# Revit family: BTSMP-LMI
name_source: partatom
category: Communication Devices
revit_build: Autodesk Revit 2014 (Build: 20130308_1515(x64)
units: mm (PartAtom-declared; Revit-internal decimal feet)

## types (1)
- BTSMP
    Assembly Code = D5090
    Black = Paint - Hubbell - Carbon Black
    Certifications = • Conforms with UL STD 508, UL STD 244A
    Coverage = 1:1 (Mounting Height : Coverage Radius);
Up to 14ft
    Default Elevation = 48 "
    Description = The Passive-Infrared Bluetooth sensor module, or BTSMP, is the newest series of the Hubbell Control Solutions Bluetooth Sensor family. Perfect for architectural applications, it is smaller, more cost effective, seamlessly integrates with all luminaires and provides simple dimming control using the controlHUBB app.
    Features = Passive Infrared (PIR) sensing technology provides excellent major
motion detection
• Wireless programming using HCS controlHUBB mobile app
• 0-10V dimming control
• Single/Dual motion sensor timer modes
• Daylight sensor with multiple daylight harvesting modes
• Compact, discrete, low profile fixture sensor
    Manufacturer = Hubbell Control Solutions
    Model = Low Mount Indoor Sensor Module
    Mounting = Up to 14 ft
    Product Documentation Link = https://hubbellcdn.com
    Product Page URL = https://www.hubbell.com
    Sensor Type = Passive Infrared
    Type Comments = Bluetooth® Low Mount Indoor Sensor Module
    URL = https://www.hubbell.com
    Warranty = 5-Years Warranty
    White = Paint - Hubbell - Matte White
    Width = 1.6 "

## geometry (parser evidence)
native form markers: Sweep x1
no freeform markers — native parametric forms only
